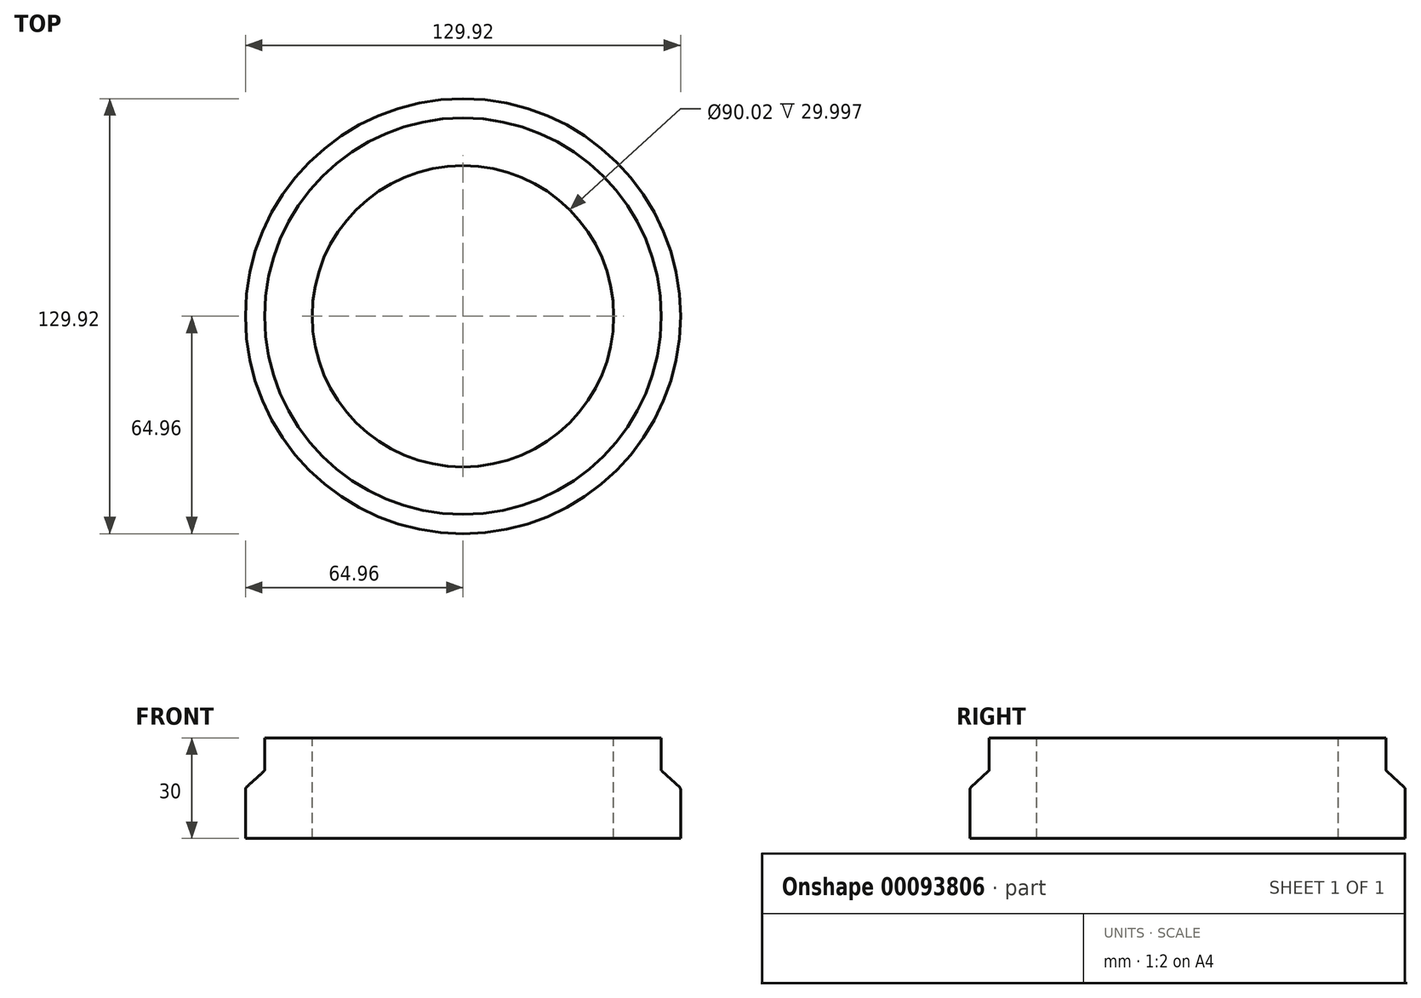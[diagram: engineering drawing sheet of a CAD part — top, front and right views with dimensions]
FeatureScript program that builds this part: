
annotation { "Feature Type Name" : "Feature", "Feature Type Description" : "" }
export const myFeature = defineFeature(function(context is Context, id is Id, definition is map)
    precondition{}
    {
        {
            var Q0;
            Q0=qCreatedBy(makeId("Front.planeOp"),FACE);
            var sketch = newSketch(context, id + "F0", { "sketchPlane" : qUnion([Q0])});
            skLineSegment(sketch, "E0", {"start": v(59.2, 15) * mm, "end": v(59.2, 5.3) * mm});
            skLineSegment(sketch, "E1", {"start": v(59.2, 5.3) * mm, "end": v(64.96, 0) * mm});
            skLineSegment(sketch, "E2", {"start": v(64.96, 0) * mm, "end": v(64.96, -15) * mm});
            skLineSegment(sketch, "E3", {"start": v(64.96, -15) * mm, "end": v(45, -15) * mm});
            skLineSegment(sketch, "E4", {"start": v(45, -15) * mm, "end": v(45, 15) * mm});
            skLineSegment(sketch, "E5", {"start": v(45, 15) * mm, "end": v(59.2, 15) * mm});
            skSolve(sketch);
        }
        {
            var Q0;
            Q0=qCreatedBy(makeId("Front.planeOp"),FACE);
            var sketch = newSketch(context, id + "F1", { "sketchPlane" : qUnion([Q0])});
            skLineSegment(sketch, "E6", {"start": v(0, 18.9) * mm, "end": v(0, -15.04) * mm});
            skSolve(sketch);
        }
        {
            var Q0;
            Q0=makeQuery(id+"F0.imprint","IMPRINT",FACE,{"disambiguationData":[TD([[makeQuery(id+"F0.imprint","IMPRINT",EDGE,{"derivedFrom":sQuery(id+"F0.wireOp",EDGE,"E0")}),-1.0]])]});
            var Q1;
            Q1=sQuery(id+"F1.wireOp",EDGE,"E6");
            revolve(context, id + "F2", {"entities" : qUnion([Q0]), "axis" : qUnion([Q1]), "revolveType" : RevolveType.FULL});
        }
        {
            var Q0;
            Q0=makeQuery(id+"F2.opRevolve","SWEPT_EDGE",EDGE,{"disambiguationData":[OSD([sQuery(id+"F0.wireOp",EDGE,"E0"),sQuery(id+"F0.wireOp",EDGE,"E1")])]});
            var Q1;
            Q1=makeQuery(id+"F2.opRevolve","SWEPT_EDGE",EDGE,{"disambiguationData":[OSD([sQuery(id+"F0.wireOp",EDGE,"E1"),sQuery(id+"F0.wireOp",EDGE,"E2")])]});
            fillet(context, id + "F3", {"entities" : qUnion([Q0, Q1]), "radius" : 0.76 * mm, "tangentPropagation" : true, "allowEdgeOverflow" : false});
        }
    });
